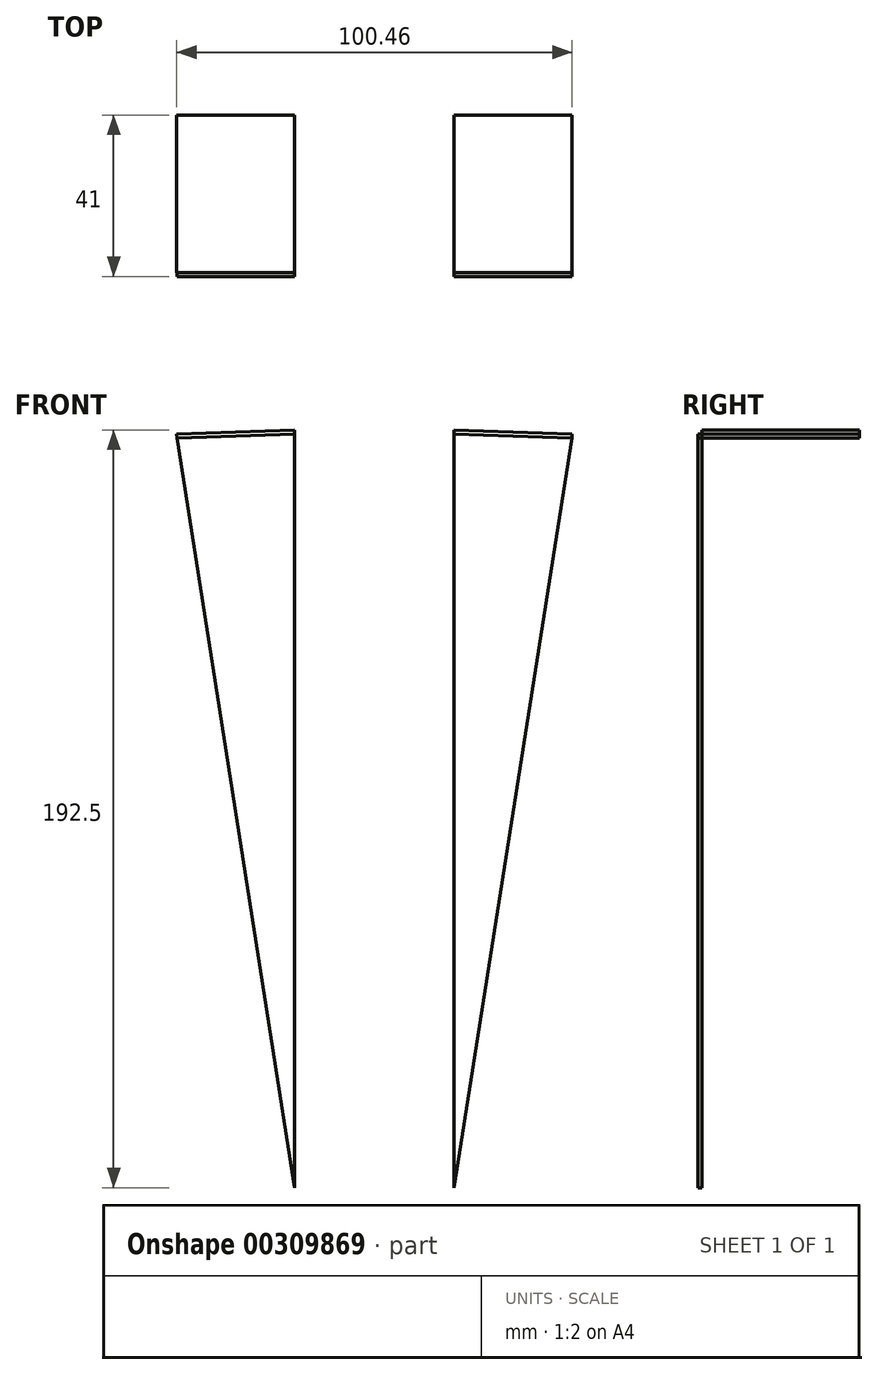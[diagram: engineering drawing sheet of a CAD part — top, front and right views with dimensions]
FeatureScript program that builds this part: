
annotation { "Feature Type Name" : "Feature", "Feature Type Description" : "" }
export const myFeature = defineFeature(function(context is Context, id is Id, definition is map)
    precondition{}
    {
        {
            var Q0;
            Q0=qCreatedBy(makeId("Front.planeOp"),FACE);
            var sketch = newSketch(context, id + "F0", { "sketchPlane" : qUnion([Q0])});
            skLineSegment(sketch, "E0.bottom", {"start": v(19.25, -95.25) * mm, "end": v(-19.25, -95.25) * mm});
            skLineSegment(sketch, "E0.top", {"start": v(19.25, 95.25) * mm, "end": v(-19.25, 95.25) * mm});
            skLineSegment(sketch, "E0.left", {"start": v(19.25, -95.25) * mm, "end": v(19.25, 95.25) * mm});
            skLineSegment(sketch, "E0.right", {"start": v(-19.25, -95.25) * mm, "end": v(-19.25, 95.25) * mm});
            skPoint(sketch, "E0.middle", {"position": v(0, 0) * mm});
            skLineSegment(sketch, "E1.0", {"start": v(20.25, 96.25) * mm, "end": v(-20.25, 96.25) * mm});
            skLineSegment(sketch, "E1.1", {"start": v(20.25, -96.25) * mm, "end": v(20.25, 96.25) * mm});
            skLineSegment(sketch, "E1.2", {"start": v(20.25, -96.25) * mm, "end": v(-20.25, -96.25) * mm});
            skLineSegment(sketch, "E1.3", {"start": v(-20.25, -96.25) * mm, "end": v(-20.25, 96.25) * mm});
            skLineSegment(sketch, "E2", {"start": v(20.25, 96.25) * mm, "end": v(50.23, 95.25) * mm});
            skLineSegment(sketch, "E3", {"start": v(-20.25, 96.25) * mm, "end": v(-50.23, 95.25) * mm});
            skLineSegment(sketch, "E4", {"start": v(50.23, 95.25) * mm, "end": v(50.2, 94.25) * mm});
            skLineSegment(sketch, "E5", {"start": v(50.2, 94.25) * mm, "end": v(20.25, -96.25) * mm});
            skLineSegment(sketch, "E6.MirrorCS", {"start": v(-50.23, 95.25) * mm, "end": v(-50.2, 94.25) * mm});
            skLineSegment(sketch, "E7.MirrorCS", {"start": v(-50.2, 94.25) * mm, "end": v(-20.25, -96.25) * mm});
            skLineSegment(sketch, "E8", {"start": v(50.2, 94.25) * mm, "end": v(20.25, 95.25) * mm});
            skLineSegment(sketch, "E9", {"start": v(-50.2, 94.25) * mm, "end": v(-20.25, 95.25) * mm});
            skSolve(sketch);
        }
        {
            var Q0;
            {var subQ0=sQuery(id+"F0.wireOp",EDGE,"E5");Q0=makeQuery(id+"F0.imprint","IMPRINT",FACE,{"disambiguationData":[TD([[makeQuery(id+"F0.imprint","IMPRINT",EDGE,{"derivedFrom":subQ0}),-1.0]])]});}
            var Q1;
            {var subQ0=sQuery(id+"F0.wireOp",EDGE,"E7.MirrorCS");Q1=makeQuery(id+"F0.imprint","IMPRINT",FACE,{"disambiguationData":[TD([[makeQuery(id+"F0.imprint","IMPRINT",EDGE,{"derivedFrom":subQ0}),1.0]])]});}
            extrude(context, id + "F1", {"entities" : qUnion([Q0, Q1]), "depth" : 1 * mm});
        }
        {
            var Q0;
            {var subQ0=sQuery(id+"F0.wireOp",EDGE,"E2");Q0=makeQuery(id+"F0.imprint","IMPRINT",FACE,{"disambiguationData":[TD([[makeQuery(id+"F0.imprint","IMPRINT",EDGE,{"derivedFrom":subQ0}),-1.0]])]});}
            var Q1;
            Q1=makeQuery(id+"F0.imprint","IMPRINT",FACE,{"disambiguationData":[TD([[makeQuery(id+"F0.imprint","IMPRINT",EDGE,{"derivedFrom":sQuery(id+"F0.wireOp",EDGE,"E6.MirrorCS")}),1.0]])]});
            extrude(context, id + "F2", {"entities" : qUnion([Q0, Q1]), "oppositeDirection" : true, "depth" : 40 * mm});
        }
    });
